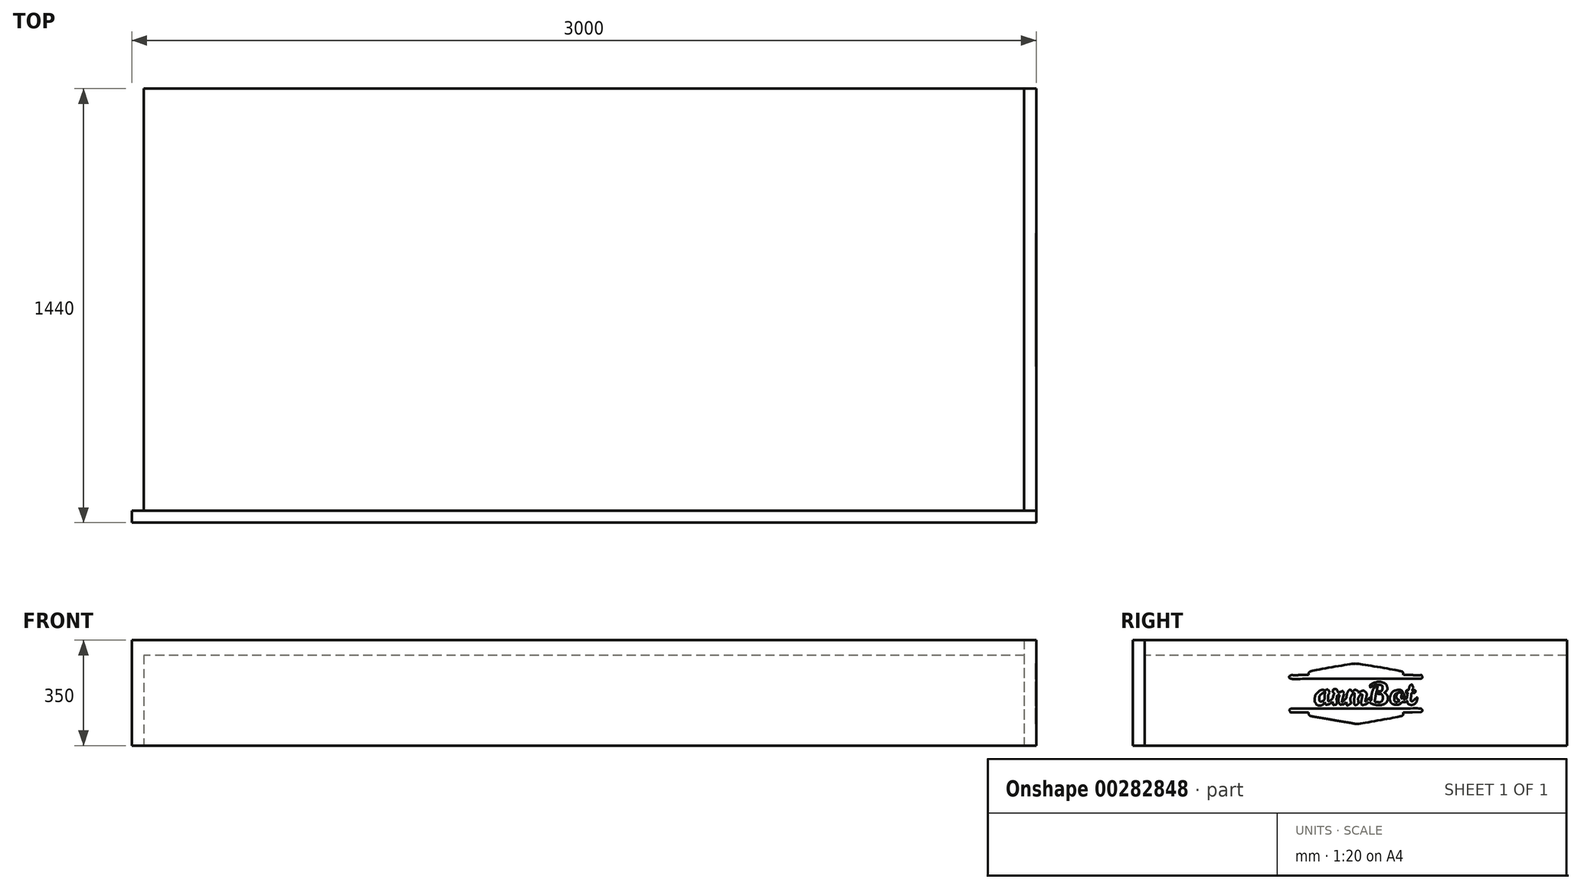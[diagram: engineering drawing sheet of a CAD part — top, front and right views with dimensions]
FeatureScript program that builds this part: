
annotation { "Feature Type Name" : "Feature", "Feature Type Description" : "" }
export const myFeature = defineFeature(function(context is Context, id is Id, definition is map)
    precondition{}
    {
        {
            var Q0;
            Q0=qCreatedBy(makeId("Top.planeOp"),FACE);
            var sketch = newSketch(context, id + "F0", { "sketchPlane" : qUnion([Q0])});
            skLineSegment(sketch, "E0.bottom", {"start": v(1460, 700) * mm, "end": v(-1460, 700) * mm});
            skLineSegment(sketch, "E0.top", {"start": v(1460, -700) * mm, "end": v(-1460, -700) * mm});
            skLineSegment(sketch, "E0.left", {"start": v(1460, 700) * mm, "end": v(1460, -700) * mm});
            skLineSegment(sketch, "E0.right", {"start": v(-1460, 700) * mm, "end": v(-1460, -700) * mm});
            skPoint(sketch, "E0.middle", {"position": v(0, 0) * mm});
            skSolve(sketch);
        }
        {
            var Q0;
            Q0=qSketchRegion(id+"F0",true);
            extrude(context, id + "F1", {"entities" : qUnion([Q0]), "depth" : 300 * mm});
        }
        {
            var Q0;
            Q0=makeQuery(id+"F1.opExtrude","SWEPT_FACE",FACE,{"disambiguationData":[OSD([sQuery(id+"F0.wireOp",EDGE,"E0.left")])]});
            var sketch = newSketch(context, id + "F2", { "sketchPlane" : qUnion([Q0])});
            skLineSegment(sketch, "E1.bottom", {"start": v(-700, 0) * mm, "end": v(700, 0) * mm});
            skLineSegment(sketch, "E1.top", {"start": v(-700, 350) * mm, "end": v(700, 350) * mm});
            skLineSegment(sketch, "E1.left", {"start": v(-700, 0) * mm, "end": v(-700, 350) * mm});
            skLineSegment(sketch, "E1.right", {"start": v(700, 0) * mm, "end": v(700, 350) * mm});
            skSolve(sketch);
        }
        {
            var Q0;
            Q0=qSketchRegion(id+"F2",true);
            extrude(context, id + "F3", {"entities" : qUnion([Q0]), "depth" : 40 * mm});
        }
        {
            var Q0;
            Q0=makeQuery(id+"F1.opExtrude","SWEPT_FACE",FACE,{"disambiguationData":[OSD([sQuery(id+"F0.wireOp",EDGE,"E0.top")])]});
            var sketch = newSketch(context, id + "F4", { "sketchPlane" : qUnion([Q0])});
            skLineSegment(sketch, "E2.bottom", {"start": v(-1500, 350) * mm, "end": v(1500, 350) * mm});
            skLineSegment(sketch, "E2.top", {"start": v(-1500, 0) * mm, "end": v(1500, 0) * mm});
            skLineSegment(sketch, "E2.left", {"start": v(-1500, 350) * mm, "end": v(-1500, 0) * mm});
            skLineSegment(sketch, "E2.right", {"start": v(1500, 350) * mm, "end": v(1500, 0) * mm});
            skSolve(sketch);
        }
        {
            var Q0;
            Q0=qSketchRegion(id+"F4",true);
            extrude(context, id + "F5", {"entities" : qUnion([Q0]), "depth" : 40 * mm});
        }
        {
            var Q0;
            Q0=makeQuery(id+"F1.opExtrude","CAP_FACE",FACE,{"disambiguationData":[OSD([sQuery(id+"F0.wireOp",EDGE,"E0.bottom"),sQuery(id+"F0.wireOp",EDGE,"E0.top"),sQuery(id+"F0.wireOp",EDGE,"E0.left"),sQuery(id+"F0.wireOp",EDGE,"E0.right")])],"isStart":false});
            var sketch = newSketch(context, id + "F6", { "sketchPlane" : qUnion([Q0])});
            skFitSpline(sketch, "E3", {"points": [v(-9.76, -247.93) * mm, v(-14.36, -247) * mm, v(-98.7, -232.48) * mm, v(-197.18, -215.67) * mm]});
            skFitSpline(sketch, "E4", {"points": [v(-197.18, -215.67) * mm, v(-303.5, -197.52) * mm, v(-377.79, -184.02) * mm, v(-380.05, -182.43) * mm]});
            skFitSpline(sketch, "E5", {"points": [v(-380.05, -182.43) * mm, v(-386.35, -178.01) * mm, v(-389.22, -172.54) * mm, v(-390.38, -162.7) * mm]});
            skLineSegment(sketch, "E6", {"start": v(-390.38, -162.7) * mm, "end": v(-391.49, -153.38) * mm});
            skLineSegment(sketch, "E7", {"start": v(-391.49, -153.38) * mm, "end": v(-463.29, -153.35) * mm});
            skFitSpline(sketch, "E8", {"points": [v(-463.29, -153.35) * mm, v(-540.74, -153.32) * mm, v(-542.21, -153.15) * mm, v(-546.84, -143.5) * mm]});
            skFitSpline(sketch, "E9", {"points": [v(-546.84, -143.5) * mm, v(-550.32, -136.23) * mm, v(-547.5, -129.03) * mm, v(-539.62, -125.02) * mm]});
            skFitSpline(sketch, "E10", {"points": [v(-539.62, -125.02) * mm, v(-533.58, -121.95) * mm, v(-503.94, -121.77) * mm, v(0.65, -121.77) * mm]});
            skFitSpline(sketch, "E11", {"points": [v(0.65, -121.77) * mm, v(385.66, -121.76) * mm, v(536.18, -122.34) * mm, v(540.43, -123.82) * mm]});
            skFitSpline(sketch, "E12", {"points": [v(540.43, -123.82) * mm, v(543.67, -124.95) * mm, v(547.14, -127.4) * mm, v(548.14, -129.27) * mm]});
            skFitSpline(sketch, "E13", {"points": [v(548.14, -129.27) * mm, v(551.05, -134.7) * mm, v(550.26, -143.3) * mm, v(546.41, -148.06) * mm]});
            skLineSegment(sketch, "E14", {"start": v(546.41, -148.06) * mm, "end": v(542.86, -152.45) * mm});
            skLineSegment(sketch, "E15", {"start": v(542.86, -152.45) * mm, "end": v(467.85, -153.38) * mm});
            skLineSegment(sketch, "E16", {"start": v(467.85, -153.38) * mm, "end": v(392.83, -154.3) * mm});
            skLineSegment(sketch, "E17", {"start": v(392.83, -154.3) * mm, "end": v(392.5, -162.05) * mm});
            skFitSpline(sketch, "E18", {"points": [v(392.5, -162.05) * mm, v(391.99, -173.78) * mm, v(387.68, -180.46) * mm, v(378.46, -183.85) * mm]});
            skFitSpline(sketch, "E19", {"points": [v(378.46, -183.85) * mm, v(371.97, -186.24) * mm, v(2.57, -250.58) * mm, v(-0.47, -249.85) * mm]});
            skFitSpline(sketch, "E20", {"points": [v(-0.47, -249.85) * mm, v(-0.98, -249.73) * mm, v(-5.16, -248.87) * mm, v(-9.76, -247.93) * mm]});
            skLineSegment(sketch, "E21", {"start": v(-9.76, -247.93) * mm, "end": v(-9.76, -247.93) * mm});
            skFitSpline(sketch, "E22", {"points": [v(163.18, -91.34) * mm, v(144.56, -86.99) * mm, v(127.82, -80.58) * mm, v(118.25, -74.15) * mm]});
            skLineSegment(sketch, "E23", {"start": v(118.25, -74.15) * mm, "end": v(108.82, -67.8) * mm});
            skLineSegment(sketch, "E24", {"start": v(108.82, -67.8) * mm, "end": v(101.7, -74.22) * mm});
            skFitSpline(sketch, "E25", {"points": [v(101.7, -74.22) * mm, v(92.92, -82.15) * mm, v(86.06, -85.78) * mm, v(75.22, -88.2) * mm]});
            skFitSpline(sketch, "E26", {"points": [v(75.22, -88.2) * mm, v(52.86, -93.22) * mm, v(44.33, -75.76) * mm, v(50.52, -37.64) * mm]});
            skFitSpline(sketch, "E27", {"points": [v(50.52, -37.64) * mm, v(54.63, -12.34) * mm, v(54.44, -8.7) * mm, v(48.9, -6.17) * mm]});
            skFitSpline(sketch, "E28", {"points": [v(48.9, -6.17) * mm, v(42.7, -3.35) * mm, v(36.64, -7.44) * mm, v(29.87, -18.99) * mm]});
            skFitSpline(sketch, "E29", {"points": [v(29.87, -18.99) * mm, v(21.01, -34.1) * mm, v(18.43, -44.15) * mm, v(20.53, -55.3) * mm]});
            skFitSpline(sketch, "E30", {"points": [v(20.53, -55.3) * mm, v(21.54, -60.66) * mm, v(22.46, -68.35) * mm, v(22.57, -72.38) * mm]});
            skFitSpline(sketch, "E31", {"points": [v(22.57, -72.38) * mm, v(22.76, -78.97) * mm, v(22, -80.26) * mm, v(14.95, -85.23) * mm]});
            skFitSpline(sketch, "E32", {"points": [v(14.95, -85.23) * mm, v(4.39, -92.68) * mm, v(-7.54, -93.24) * mm, v(-11.04, -86.43) * mm]});
            skFitSpline(sketch, "E33", {"points": [v(-11.04, -86.43) * mm, v(-13.95, -80.76) * mm, v(-14.16, -56.28) * mm, v(-11.54, -26.93) * mm]});
            skFitSpline(sketch, "E34", {"points": [v(-11.54, -26.93) * mm, v(-9.2, -0.66) * mm, v(-9.84, 2.83) * mm, v(-17.07, 2.83) * mm]});
            skFitSpline(sketch, "E35", {"points": [v(-17.07, 2.83) * mm, v(-23.9, 2.83) * mm, v(-30.46, -4.7) * mm, v(-38.87, -22.23) * mm]});
            skFitSpline(sketch, "E36", {"points": [v(-38.87, -22.23) * mm, v(-45.93, -36.93) * mm, v(-46.62, -45.33) * mm, v(-42.27, -63.77) * mm]});
            skFitSpline(sketch, "E37", {"points": [v(-42.27, -63.77) * mm, v(-38.91, -78.01) * mm, v(-39.9, -80.3) * mm, v(-52.19, -87) * mm]});
            skFitSpline(sketch, "E38", {"points": [v(-52.19, -87) * mm, v(-68.26, -95.75) * mm, v(-75.2, -92.86) * mm, v(-77.56, -76.43) * mm]});
            skLineSegment(sketch, "E39", {"start": v(-77.56, -76.43) * mm, "end": v(-78.86, -67.36) * mm});
            skLineSegment(sketch, "E40", {"start": v(-78.86, -67.36) * mm, "end": v(-86.62, -74.83) * mm});
            skFitSpline(sketch, "E41", {"points": [v(-86.62, -74.83) * mm, v(-97.05, -84.9) * mm, v(-104.92, -88.54) * mm, v(-116.78, -88.82) * mm]});
            skFitSpline(sketch, "E42", {"points": [v(-116.78, -88.82) * mm, v(-128.34, -89.1) * mm, v(-132.94, -86) * mm, v(-138.3, -74.35) * mm]});
            skFitSpline(sketch, "E43", {"points": [v(-138.3, -74.35) * mm, v(-144.12, -61.65) * mm, v(-141.58, -31.54) * mm, v(-133.32, -15.58) * mm]});
            skLineSegment(sketch, "E44", {"start": v(-133.32, -15.58) * mm, "end": v(-130.44, -10) * mm});
            skLineSegment(sketch, "E45", {"start": v(-130.44, -10) * mm, "end": v(-141.2, -10.56) * mm});
            skLineSegment(sketch, "E46", {"start": v(-141.2, -10.56) * mm, "end": v(-151.94, -11.12) * mm});
            skLineSegment(sketch, "E47", {"start": v(-151.94, -11.12) * mm, "end": v(-155.34, -25.07) * mm});
            skFitSpline(sketch, "E48", {"points": [v(-155.34, -25.07) * mm, v(-157.97, -35.9) * mm, v(-158.52, -43.56) * mm, v(-157.8, -59.34) * mm]});
            skFitSpline(sketch, "E49", {"points": [v(-157.8, -59.34) * mm, v(-157.29, -70.85) * mm, v(-157.67, -81.12) * mm, v(-158.7, -83.03) * mm]});
            skFitSpline(sketch, "E50", {"points": [v(-158.7, -83.03) * mm, v(-161.25, -87.81) * mm, v(-170.24, -92.01) * mm, v(-177.92, -92.01) * mm]});
            skFitSpline(sketch, "E51", {"points": [v(-177.92, -92.01) * mm, v(-186.08, -92.01) * mm, v(-189.42, -87.45) * mm, v(-191.2, -73.87) * mm]});
            skLineSegment(sketch, "E52", {"start": v(-191.2, -73.87) * mm, "end": v(-192.48, -64.09) * mm});
            skLineSegment(sketch, "E53", {"start": v(-192.48, -64.09) * mm, "end": v(-200.42, -71.4) * mm});
            skFitSpline(sketch, "E54", {"points": [v(-200.42, -71.4) * mm, v(-209.89, -80.13) * mm, v(-220.17, -85.65) * mm, v(-231.87, -88.27) * mm]});
            skFitSpline(sketch, "E55", {"points": [v(-231.87, -88.27) * mm, v(-243.7, -90.92) * mm, v(-250.08, -87.49) * mm, v(-254.4, -76.16) * mm]});
            skLineSegment(sketch, "E56", {"start": v(-254.4, -76.16) * mm, "end": v(-257.65, -67.68) * mm});
            skLineSegment(sketch, "E57", {"start": v(-257.65, -67.68) * mm, "end": v(-262.94, -74.1) * mm});
            skFitSpline(sketch, "E58", {"points": [v(-262.94, -74.1) * mm, v(-279.38, -94.04) * mm, v(-316.37, -95.84) * mm, v(-331.85, -77.45) * mm]});
            skFitSpline(sketch, "E59", {"points": [v(-331.85, -77.45) * mm, v(-339.17, -68.75) * mm, v(-341.42, -59.86) * mm, v(-340.14, -44.75) * mm]});
            skFitSpline(sketch, "E60", {"points": [v(-340.14, -44.75) * mm, v(-338.13, -20.94) * mm, v(-329.14, -1.86) * mm, v(-313.1, 12.61) * mm]});
            skFitSpline(sketch, "E61", {"points": [v(-313.1, 12.61) * mm, v(-297.94, 26.32) * mm, v(-276.95, 32.69) * mm, v(-259.7, 28.82) * mm]});
            skFitSpline(sketch, "E62", {"points": [v(-259.7, 28.82) * mm, v(-252.55, 27.22) * mm, v(-250.45, 27.38) * mm, v(-247.85, 29.73) * mm]});
            skFitSpline(sketch, "E63", {"points": [v(-247.85, 29.73) * mm, v(-240.93, 36) * mm, v(-226.99, 30.32) * mm, v(-220.73, 18.7) * mm]});
            skLineSegment(sketch, "E64", {"start": v(-220.73, 18.7) * mm, "end": v(-217.21, 12.17) * mm});
            skLineSegment(sketch, "E65", {"start": v(-217.21, 12.17) * mm, "end": v(-223.2, 0.02) * mm});
            skFitSpline(sketch, "E66", {"points": [v(-223.2, 0.02) * mm, v(-228.92, -11.58) * mm, v(-229.19, -13.1) * mm, v(-229.16, -33.94) * mm]});
            skFitSpline(sketch, "E67", {"points": [v(-229.16, -33.94) * mm, v(-229.13, -57.9) * mm, v(-228.1, -61.48) * mm, v(-221.81, -59.49) * mm]});
            skFitSpline(sketch, "E68", {"points": [v(-221.81, -59.49) * mm, v(-215.07, -57.35) * mm, v(-188.28, -30.28) * mm, v(-188.28, -25.6) * mm]});
            skFitSpline(sketch, "E69", {"points": [v(-188.28, -25.6) * mm, v(-188.28, -23.36) * mm, v(-186.22, -15.85) * mm, v(-183.7, -8.92) * mm]});
            skFitSpline(sketch, "E70", {"points": [v(-183.7, -8.92) * mm, v(-179.26, 3.33) * mm, v(-179.23, 3.78) * mm, v(-182.54, 7.44) * mm]});
            skFitSpline(sketch, "E71", {"points": [v(-182.54, 7.44) * mm, v(-188.48, 13.98) * mm, v(-190.53, 19.67) * mm, v(-189.3, 26.21) * mm]});
            skFitSpline(sketch, "E72", {"points": [v(-189.3, 26.21) * mm, v(-187.82, 34.15) * mm, v(-182.12, 38.16) * mm, v(-172.31, 38.16) * mm]});
            skFitSpline(sketch, "E73", {"points": [v(-172.31, 38.16) * mm, v(-163.16, 38.16) * mm, v(-156.23, 32.34) * mm, v(-150.73, 20.03) * mm]});
            skFitSpline(sketch, "E74", {"points": [v(-150.73, 20.03) * mm, v(-147.7, 13.24) * mm, v(-146.4, 12.12) * mm, v(-141.55, 12.12) * mm]});
            skFitSpline(sketch, "E75", {"points": [v(-141.55, 12.12) * mm, v(-138.45, 12.12) * mm, v(-130.4, 14.33) * mm, v(-123.66, 17.03) * mm]});
            skFitSpline(sketch, "E76", {"points": [v(-123.66, 17.03) * mm, v(-109.3, 22.78) * mm, v(-107.41, 22.17) * mm, v(-101.2, 9.8) * mm]});
            skLineSegment(sketch, "E77", {"start": v(-101.2, 9.8) * mm, "end": v(-96.87, 1.18) * mm});
            skLineSegment(sketch, "E78", {"start": v(-96.87, 1.18) * mm, "end": v(-104.6, -26.95) * mm});
            skFitSpline(sketch, "E79", {"points": [v(-104.6, -26.95) * mm, v(-115.26, -65.72) * mm, v(-113.52, -68.38) * mm, v(-91.12, -47.46) * mm]});
            skLineSegment(sketch, "E80", {"start": v(-91.12, -47.46) * mm, "end": v(-77.26, -34.51) * mm});
            skLineSegment(sketch, "E81", {"start": v(-77.26, -34.51) * mm, "end": v(-76.15, -22.7) * mm});
            skFitSpline(sketch, "E82", {"points": [v(-76.15, -22.7) * mm, v(-74.76, -7.77) * mm, v(-68.68, 10.87) * mm, v(-61.04, 23.61) * mm]});
            skFitSpline(sketch, "E83", {"points": [v(-61.04, 23.61) * mm, v(-56.21, 31.68) * mm, v(-54.07, 33.61) * mm, v(-49.45, 34.07) * mm]});
            skFitSpline(sketch, "E84", {"points": [v(-49.45, 34.07) * mm, v(-44.95, 34.52) * mm, v(-42.63, 33.32) * mm, v(-38.15, 28.2) * mm]});
            skFitSpline(sketch, "E85", {"points": [v(-38.15, 28.2) * mm, v(-35.04, 24.67) * mm, v(-32.16, 20.74) * mm, v(-31.73, 19.46) * mm]});
            skFitSpline(sketch, "E86", {"points": [v(-31.73, 19.46) * mm, v(-31.21, 17.9) * mm, v(-28.37, 19.02) * mm, v(-23, 22.9) * mm]});
            skFitSpline(sketch, "E87", {"points": [v(-23, 22.9) * mm, v(-11.96, 30.9) * mm, v(-1.17, 32.3) * mm, v(9.54, 27.1) * mm]});
            skFitSpline(sketch, "E88", {"points": [v(9.54, 27.1) * mm, v(18.23, 22.9) * mm, v(22.7, 17.7) * mm, v(24.79, 9.4) * mm]});
            skLineSegment(sketch, "E89", {"start": v(24.79, 9.4) * mm, "end": v(26.04, 4.44) * mm});
            skLineSegment(sketch, "E90", {"start": v(26.04, 4.44) * mm, "end": v(30.92, 9.1) * mm});
            skFitSpline(sketch, "E91", {"points": [v(30.92, 9.1) * mm, v(43.6, 21.22) * mm, v(66.06, 25.1) * mm, v(77.8, 17.18) * mm]});
            skFitSpline(sketch, "E92", {"points": [v(77.8, 17.18) * mm, v(81.26, 14.85) * mm, v(85.14, 10.88) * mm, v(86.42, 8.35) * mm]});
            skFitSpline(sketch, "E93", {"points": [v(86.42, 8.35) * mm, v(90.04, 1.18) * mm, v(89.21, -14.95) * mm, v(84.14, -35.88) * mm]});
            skFitSpline(sketch, "E94", {"points": [v(84.14, -35.88) * mm, v(81.59, -46.43) * mm, v(79.5, -56.26) * mm, v(79.5, -57.73) * mm]});
            skFitSpline(sketch, "E95", {"points": [v(79.5, -57.73) * mm, v(79.5, -63.6) * mm, v(86.26, -59.69) * mm, v(100.97, -45.33) * mm]});
            skFitSpline(sketch, "E96", {"points": [v(100.97, -45.33) * mm, v(110.63, -35.9) * mm, v(117.25, -30.77) * mm, v(118.65, -31.64) * mm]});
            skFitSpline(sketch, "E97", {"points": [v(118.65, -31.64) * mm, v(120.17, -32.58) * mm, v(120.56, -36.5) * mm, v(119.89, -43.92) * mm]});
            skFitSpline(sketch, "E98", {"points": [v(119.89, -43.92) * mm, v(118.95, -54.29) * mm, v(119.1, -54.82) * mm, v(123.1, -54.82) * mm]});
            skFitSpline(sketch, "E99", {"points": [v(123.1, -54.82) * mm, v(127.02, -54.82) * mm, v(127.36, -53.84) * mm, v(128.4, -39.48) * mm]});
            skFitSpline(sketch, "E100", {"points": [v(128.4, -39.48) * mm, v(130.72, -7.09) * mm, v(148.03, 43.77) * mm, v(160.6, 55.09) * mm]});
            skFitSpline(sketch, "E101", {"points": [v(160.6, 55.09) * mm, v(178.01, 70.78) * mm, v(179.9, 58.14) * mm, v(168.42, 2.83) * mm]});
            skFitSpline(sketch, "E102", {"points": [v(168.42, 2.83) * mm, v(163.73, -19.8) * mm, v(158.67, -63.5) * mm, v(160.5, -65.68) * mm]});
            skFitSpline(sketch, "E103", {"points": [v(160.5, -65.68) * mm, v(161.76, -67.18) * mm, v(175.96, -69.61) * mm, v(183.63, -69.64) * mm]});
            skFitSpline(sketch, "E104", {"points": [v(183.63, -69.64) * mm, v(200.98, -69.71) * mm, v(215.69, -61.64) * mm, v(220.83, -49.22) * mm]});
            skFitSpline(sketch, "E105", {"points": [v(220.83, -49.22) * mm, v(224.51, -40.34) * mm, v(222.43, -16.02) * mm, v(217.28, -7.68) * mm]});
            skFitSpline(sketch, "E106", {"points": [v(217.28, -7.68) * mm, v(213.13, -0.96) * mm, v(212.95, -0.9) * mm, v(200.63, -0.9) * mm]});
            skFitSpline(sketch, "E107", {"points": [v(200.63, -0.9) * mm, v(187.27, -0.9) * mm, v(181.1, 1.8) * mm, v(179.39, 8.35) * mm]});
            skFitSpline(sketch, "E108", {"points": [v(179.39, 8.35) * mm, v(178.82, 10.5) * mm, v(179.82, 13.89) * mm, v(181.7, 16.2) * mm]});
            skFitSpline(sketch, "E109", {"points": [v(181.7, 16.2) * mm, v(184.4, 19.56) * mm, v(187.56, 20.46) * mm, v(199.63, 21.31) * mm]});
            skFitSpline(sketch, "E110", {"points": [v(199.63, 21.31) * mm, v(213.63, 22.3) * mm, v(214.4, 22.6) * mm, v(217.02, 27.93) * mm]});
            skFitSpline(sketch, "E111", {"points": [v(217.02, 27.93) * mm, v(218.53, 31) * mm, v(219.77, 38.53) * mm, v(219.78, 44.67) * mm]});
            skFitSpline(sketch, "E112", {"points": [v(219.78, 44.67) * mm, v(219.8, 64.17) * mm, v(211.17, 71.67) * mm, v(187.07, 73.1) * mm]});
            skFitSpline(sketch, "E113", {"points": [v(187.07, 73.1) * mm, v(170.05, 74.11) * mm, v(157.7, 71.45) * mm, v(139.99, 62.97) * mm]});
            skFitSpline(sketch, "E114", {"points": [v(139.99, 62.97) * mm, v(124.82, 55.7) * mm, v(118.55, 54.98) * mm, v(118.55, 60.51) * mm]});
            skFitSpline(sketch, "E115", {"points": [v(118.55, 60.51) * mm, v(118.55, 70.5) * mm, v(143.11, 88.38) * mm, v(165.9, 94.95) * mm]});
            skFitSpline(sketch, "E116", {"points": [v(165.9, 94.95) * mm, v(181.16, 99.36) * mm, v(211.58, 97.92) * mm, v(227.33, 92.04) * mm]});
            skFitSpline(sketch, "E117", {"points": [v(227.33, 92.04) * mm, v(241.91, 86.6) * mm, v(254.67, 73.92) * mm, v(257.71, 61.83) * mm]});
            skFitSpline(sketch, "E118", {"points": [v(257.71, 61.83) * mm, v(262.48, 42.9) * mm, v(259.33, 31.38) * mm, v(245.79, 18.17) * mm]});
            skFitSpline(sketch, "E119", {"points": [v(245.79, 18.17) * mm, v(240.28, 12.8) * mm, v(236.48, 8.4) * mm, v(237.34, 8.4) * mm]});
            skFitSpline(sketch, "E120", {"points": [v(237.34, 8.4) * mm, v(241.01, 8.4) * mm, v(256.17, -7.19) * mm, v(259.81, -14.71) * mm]});
            skFitSpline(sketch, "E121", {"points": [v(259.81, -14.71) * mm, v(265.46, -26.39) * mm, v(265.68, -49.04) * mm, v(260.25, -59.68) * mm]});
            skFitSpline(sketch, "E122", {"points": [v(260.25, -59.68) * mm, v(254.38, -71.16) * mm, v(239.5, -83.55) * mm, v(225.92, -88.28) * mm]});
            skFitSpline(sketch, "E123", {"points": [v(225.92, -88.28) * mm, v(211.44, -93.33) * mm, v(178.53, -94.93) * mm, v(163.18, -91.34) * mm]});
            skFitSpline(sketch, "E124", {"points": [v(-281.84, -62.14) * mm, v(-267.85, -56.85) * mm, v(-259.05, -41.8) * mm, v(-258.98, -23.08) * mm]});
            skFitSpline(sketch, "E125", {"points": [v(-258.98, -23.08) * mm, v(-258.96, -16.37) * mm, v(-258.05, -6.04) * mm, v(-256.95, -0.12) * mm]});
            skFitSpline(sketch, "E126", {"points": [v(-256.95, -0.12) * mm, v(-255.86, 5.8) * mm, v(-255.42, 11.09) * mm, v(-255.98, 11.64) * mm]});
            skFitSpline(sketch, "E127", {"points": [v(-255.98, 11.64) * mm, v(-257.93, 13.6) * mm, v(-273.99, 6.15) * mm, v(-282.7, -0.75) * mm]});
            skFitSpline(sketch, "E128", {"points": [v(-282.7, -0.75) * mm, v(-295.24, -10.66) * mm, v(-302.1, -24.16) * mm, v(-303.18, -41.06) * mm]});
            skFitSpline(sketch, "E129", {"points": [v(-303.18, -41.06) * mm, v(-303.98, -53.62) * mm, v(-303.72, -54.84) * mm, v(-299.24, -59.32) * mm]});
            skFitSpline(sketch, "E130", {"points": [v(-299.24, -59.32) * mm, v(-294.03, -64.53) * mm, v(-289.93, -65.2) * mm, v(-281.84, -62.14) * mm]});
            skFitSpline(sketch, "E131", {"points": [v(-459.3, -89.94) * mm, v(-464.48, -84.62) * mm, v(-460.7, -35.47) * mm, v(-453.32, -12.23) * mm]});
            skFitSpline(sketch, "E132", {"points": [v(-453.32, -12.23) * mm, v(-452.15, -8.52) * mm, v(-452.73, -8.33) * mm, v(-465.23, -8.33) * mm]});
            skFitSpline(sketch, "E133", {"points": [v(-465.23, -8.33) * mm, v(-476.68, -8.33) * mm, v(-478.37, -7.9) * mm, v(-478.37, -4.96) * mm]});
            skFitSpline(sketch, "E134", {"points": [v(-478.37, -4.96) * mm, v(-478.37, 0.26) * mm, v(-468.99, 8.03) * mm, v(-457.1, 12.63) * mm]});
            skLineSegment(sketch, "E135", {"start": v(-457.1, 12.63) * mm, "end": v(-446.32, 16.8) * mm});
            skLineSegment(sketch, "E136", {"start": v(-446.32, 16.8) * mm, "end": v(-438.43, 39.1) * mm});
            skFitSpline(sketch, "E137", {"points": [v(-438.43, 39.1) * mm, v(-434.08, 51.37) * mm, v(-429.87, 62.96) * mm, v(-429.07, 64.87) * mm]});
            skFitSpline(sketch, "E138", {"points": [v(-429.07, 64.87) * mm, v(-427.72, 68.05) * mm, v(-428.28, 68.22) * mm, v(-435.78, 67) * mm]});
            skFitSpline(sketch, "E139", {"points": [v(-435.78, 67) * mm, v(-447.95, 65.04) * mm, v(-458.5, 59.86) * mm, v(-467.75, 51.34) * mm]});
            skFitSpline(sketch, "E140", {"points": [v(-467.75, 51.34) * mm, v(-479.66, 40.36) * mm, v(-483.95, 41.51) * mm, v(-483.95, 55.7) * mm]});
            skFitSpline(sketch, "E141", {"points": [v(-483.95, 55.7) * mm, v(-483.95, 68.83) * mm, v(-467.73, 83.32) * mm, v(-445.28, 90.26) * mm]});
            skFitSpline(sketch, "E142", {"points": [v(-445.28, 90.26) * mm, v(-427.1, 95.87) * mm, v(-406.05, 97.33) * mm, v(-358.74, 96.25) * mm]});
            skFitSpline(sketch, "E143", {"points": [v(-358.74, 96.25) * mm, v(-311.18, 95.17) * mm, v(-311.95, 95.43) * mm, v(-317.58, 82.22) * mm]});
            skFitSpline(sketch, "E144", {"points": [v(-317.58, 82.22) * mm, v(-323.64, 68.03) * mm, v(-324, 67.91) * mm, v(-360.96, 67.88) * mm]});
            skLineSegment(sketch, "E145", {"start": v(-360.96, 67.88) * mm, "end": v(-393.76, 67.85) * mm});
            skLineSegment(sketch, "E146", {"start": v(-393.76, 67.85) * mm, "end": v(-398.66, 47.9) * mm});
            skFitSpline(sketch, "E147", {"points": [v(-398.66, 47.9) * mm, v(-401.36, 36.91) * mm, v(-403.87, 26.67) * mm, v(-404.24, 25.14) * mm]});
            skFitSpline(sketch, "E148", {"points": [v(-404.24, 25.14) * mm, v(-404.8, 22.8) * mm, v(-401.23, 22.27) * mm, v(-381.74, 21.83) * mm]});
            skFitSpline(sketch, "E149", {"points": [v(-381.74, 21.83) * mm, v(-367.15, 21.5) * mm, v(-358.1, 20.53) * mm, v(-357.28, 19.21) * mm]});
            skFitSpline(sketch, "E150", {"points": [v(-357.28, 19.21) * mm, v(-355.76, 16.75) * mm, v(-359.89, 2.02) * mm, v(-363.24, -2.01) * mm]});
            skFitSpline(sketch, "E151", {"points": [v(-363.24, -2.01) * mm, v(-365.2, -4.38) * mm, v(-369.3, -4.62) * mm, v(-389.06, -3.54) * mm]});
            skLineSegment(sketch, "E152", {"start": v(-389.06, -3.54) * mm, "end": v(-412.56, -2.27) * mm});
            skLineSegment(sketch, "E153", {"start": v(-412.56, -2.27) * mm, "end": v(-416.52, -18.78) * mm});
            skFitSpline(sketch, "E154", {"points": [v(-416.52, -18.78) * mm, v(-421.04, -37.64) * mm, v(-423.77, -53.93) * mm, v(-425.45, -72.08) * mm]});
            skFitSpline(sketch, "E155", {"points": [v(-425.45, -72.08) * mm, v(-426.44, -82.86) * mm, v(-427.3, -85.14) * mm, v(-431.33, -87.78) * mm]});
            skFitSpline(sketch, "E156", {"points": [v(-431.33, -87.78) * mm, v(-437.41, -91.77) * mm, v(-456.13, -93.2) * mm, v(-459.3, -89.94) * mm]});
            skFitSpline(sketch, "E157", {"points": [v(317.5, -88.5) * mm, v(302.9, -83.79) * mm, v(289.51, -71.3) * mm, v(285.81, -58.96) * mm]});
            skFitSpline(sketch, "E158", {"points": [v(285.81, -58.96) * mm, v(282.17, -46.8) * mm, v(284.25, -22.14) * mm, v(289.96, -9.87) * mm]});
            skFitSpline(sketch, "E159", {"points": [v(289.96, -9.87) * mm, v(299.26, 10.12) * mm, v(316.09, 24.32) * mm, v(335.9, 28.9) * mm]});
            skFitSpline(sketch, "E160", {"points": [v(335.9, 28.9) * mm, v(354.07, 33.1) * mm, v(378.44, 28.13) * mm, v(386.33, 18.63) * mm]});
            skFitSpline(sketch, "E161", {"points": [v(386.33, 18.63) * mm, v(390.02, 14.18) * mm, v(386.8, 12.82) * mm, v(369.86, 11.65) * mm]});
            skFitSpline(sketch, "E162", {"points": [v(369.86, 11.65) * mm, v(362, 11.12) * mm, v(352.6, 9.43) * mm, v(348.96, 7.91) * mm]});
            skFitSpline(sketch, "E163", {"points": [v(348.96, 7.91) * mm, v(331.95, 0.8) * mm, v(320.77, -16.17) * mm, v(320.52, -35.3) * mm]});
            skFitSpline(sketch, "E164", {"points": [v(320.52, -35.3) * mm, v(320.22, -57.93) * mm, v(334.52, -68.41) * mm, v(357.15, -62.13) * mm]});
            skLineSegment(sketch, "E165", {"start": v(357.15, -62.13) * mm, "end": v(364.23, -60.16) * mm});
            skLineSegment(sketch, "E166", {"start": v(364.23, -60.16) * mm, "end": v(357.84, -53.09) * mm});
            skFitSpline(sketch, "E167", {"points": [v(357.84, -53.09) * mm, v(336.45, -29.41) * mm, v(349.03, 6.55) * mm, v(378.7, 6.55) * mm]});
            skFitSpline(sketch, "E168", {"points": [v(378.7, 6.55) * mm, v(389.23, 6.55) * mm, v(395.06, 3.8) * mm, v(399.43, -3.17) * mm]});
            skFitSpline(sketch, "E169", {"points": [v(399.43, -3.17) * mm, v(402.65, -8.3) * mm, v(403.12, -11.47) * mm, v(402.44, -23.2) * mm]});
            skFitSpline(sketch, "E170", {"points": [v(402.44, -23.2) * mm, v(402, -30.88) * mm, v(401.02, -39.04) * mm, v(400.27, -41.34) * mm]});
            skFitSpline(sketch, "E171", {"points": [v(400.27, -41.34) * mm, v(398.58, -46.51) * mm, v(402.33, -46.92) * mm, v(411.06, -42.52) * mm]});
            skFitSpline(sketch, "E172", {"points": [v(411.06, -42.52) * mm, v(421.31, -37.33) * mm, v(425.37, -32.45) * mm, v(425.44, -25.2) * mm]});
            skFitSpline(sketch, "E173", {"points": [v(425.44, -25.2) * mm, v(425.48, -21.55) * mm, v(426.6, -12.92) * mm, v(427.94, -6.02) * mm]});
            skFitSpline(sketch, "E174", {"points": [v(427.94, -6.02) * mm, v(429.27, 0.87) * mm, v(429.94, 6.94) * mm, v(429.42, 7.46) * mm]});
            skFitSpline(sketch, "E175", {"points": [v(429.42, 7.46) * mm, v(428.9, 7.98) * mm, v(425.6, 8.4) * mm, v(422.07, 8.4) * mm]});
            skFitSpline(sketch, "E176", {"points": [v(422.07, 8.4) * mm, v(415.71, 8.4) * mm, v(415.67, 8.46) * mm, v(416.93, 15.14) * mm]});
            skFitSpline(sketch, "E177", {"points": [v(416.93, 15.14) * mm, v(418.93, 25.81) * mm, v(421.68, 28.86) * mm, v(429.3, 28.86) * mm]});
            skFitSpline(sketch, "E178", {"points": [v(429.3, 28.86) * mm, v(435.8, 28.86) * mm, v(436.17, 29.23) * mm, v(439.97, 39.55) * mm]});
            skFitSpline(sketch, "E179", {"points": [v(439.97, 39.55) * mm, v(450.84, 69.05) * mm, v(465.01, 75.94) * mm, v(473.83, 56) * mm]});
            skLineSegment(sketch, "E180", {"start": v(473.83, 56) * mm, "end": v(477.45, 47.84) * mm});
            skLineSegment(sketch, "E181", {"start": v(477.45, 47.84) * mm, "end": v(472.82, 39.75) * mm});
            skFitSpline(sketch, "E182", {"points": [v(472.82, 39.75) * mm, v(470.27, 35.3) * mm, v(468.18, 31.02) * mm, v(468.17, 30.25) * mm]});
            skFitSpline(sketch, "E183", {"points": [v(468.17, 30.25) * mm, v(468.15, 29.49) * mm, v(474, 28.86) * mm, v(481.16, 28.86) * mm]});
            skFitSpline(sketch, "E184", {"points": [v(481.16, 28.86) * mm, v(493.59, 28.86) * mm, v(494.18, 28.66) * mm, v(494.18, 24.49) * mm]});
            skFitSpline(sketch, "E185", {"points": [v(494.18, 24.49) * mm, v(494.18, 22.08) * mm, v(493.26, 17.48) * mm, v(492.14, 14.26) * mm]});
            skFitSpline(sketch, "E186", {"points": [v(492.14, 14.26) * mm, v(490.1, 8.41) * mm, v(490.07, 8.4) * mm, v(476.53, 8.4) * mm]});
            skFitSpline(sketch, "E187", {"points": [v(476.53, 8.4) * mm, v(466.58, 8.4) * mm, v(462.7, 7.7) * mm, v(461.96, 5.79) * mm]});
            skFitSpline(sketch, "E188", {"points": [v(461.96, 5.79) * mm, v(461.4, 4.35) * mm, v(459.93, -6.74) * mm, v(458.69, -18.85) * mm]});
            skFitSpline(sketch, "E189", {"points": [v(458.69, -18.85) * mm, v(456.19, -43.13) * mm, v(457.42, -58.1) * mm, v(462.05, -59.89) * mm]});
            skFitSpline(sketch, "E190", {"points": [v(462.05, -59.89) * mm, v(466.54, -61.6) * mm, v(480.7, -53.25) * mm, v(493.44, -41.34) * mm]});
            skFitSpline(sketch, "E191", {"points": [v(493.44, -41.34) * mm, v(499.73, -35.46) * mm, v(505.73, -30.65) * mm, v(506.77, -30.65) * mm]});
            skFitSpline(sketch, "E192", {"points": [v(506.77, -30.65) * mm, v(510.1, -30.65) * mm, v(511.02, -39.58) * mm, v(508.46, -47.01) * mm]});
            skFitSpline(sketch, "E193", {"points": [v(508.46, -47.01) * mm, v(500.27, -70.78) * mm, v(464.23, -93.67) * mm, v(443.63, -88.18) * mm]});
            skFitSpline(sketch, "E194", {"points": [v(443.63, -88.18) * mm, v(436.32, -86.23) * mm, v(430.49, -78.96) * mm, v(428.05, -68.77) * mm]});
            skFitSpline(sketch, "E195", {"points": [v(428.05, -68.77) * mm, v(426, -60.18) * mm, v(425.55, -59.99) * mm, v(418.25, -64.52) * mm]});
            skFitSpline(sketch, "E196", {"points": [v(418.25, -64.52) * mm, v(412.67, -68) * mm, v(408.97, -68.73) * mm, v(397.88, -68.57) * mm]});
            skFitSpline(sketch, "E197", {"points": [v(397.88, -68.57) * mm, v(384.98, -68.4) * mm, v(384.01, -68.68) * mm, v(377.5, -74.64) * mm]});
            skFitSpline(sketch, "E198", {"points": [v(377.5, -74.64) * mm, v(365.8, -85.37) * mm, v(355.8, -89.15) * mm, v(337.98, -89.6) * mm]});
            skFitSpline(sketch, "E199", {"points": [v(337.98, -89.6) * mm, v(329.28, -89.82) * mm, v(320.07, -89.33) * mm, v(317.5, -88.5) * mm]});
            skFitSpline(sketch, "E200", {"points": [v(385.7, -25.43) * mm, v(386.64, -17.46) * mm, v(386.3, -15.64) * mm, v(383.66, -14.63) * mm]});
            skFitSpline(sketch, "E201", {"points": [v(383.66, -14.63) * mm, v(379.08, -12.87) * mm, v(376.38, -16.52) * mm, v(376.67, -24.09) * mm]});
            skFitSpline(sketch, "E202", {"points": [v(376.67, -24.09) * mm, v(376.97, -32.15) * mm, v(380.4, -39.18) * mm, v(382.83, -36.75) * mm]});
            skFitSpline(sketch, "E203", {"points": [v(382.83, -36.75) * mm, v(383.78, -35.8) * mm, v(385.07, -30.7) * mm, v(385.7, -25.43) * mm]});
            skFitSpline(sketch, "E204", {"points": [v(-539.73, 126.1) * mm, v(-551.06, 131.84) * mm, v(-551, 146.27) * mm, v(-539.62, 152.05) * mm]});
            skFitSpline(sketch, "E205", {"points": [v(-539.62, 152.05) * mm, v(-533.86, 154.98) * mm, v(-526.13, 155.3) * mm, v(-462.1, 155.3) * mm]});
            skLineSegment(sketch, "E206", {"start": v(-462.1, 155.3) * mm, "end": v(-390.97, 155.3) * mm});
            skLineSegment(sketch, "E207", {"start": v(-390.97, 155.3) * mm, "end": v(-390.97, 160.85) * mm});
            skFitSpline(sketch, "E208", {"points": [v(-390.97, 160.85) * mm, v(-390.97, 170.05) * mm, v(-385.48, 181.2) * mm, v(-379.4, 184.35) * mm]});
            skFitSpline(sketch, "E209", {"points": [v(-379.4, 184.35) * mm, v(-373.17, 187.57) * mm, v(-10.28, 250.15) * mm, v(2.18, 250.15) * mm]});
            skFitSpline(sketch, "E210", {"points": [v(2.18, 250.15) * mm, v(10.33, 250.15) * mm, v(362.94, 190.41) * mm, v(375.5, 186.9) * mm]});
            skFitSpline(sketch, "E211", {"points": [v(375.5, 186.9) * mm, v(384.93, 184.27) * mm, v(391.52, 175.86) * mm, v(393.02, 164.53) * mm]});
            skLineSegment(sketch, "E212", {"start": v(393.02, 164.53) * mm, "end": v(394.24, 155.3) * mm});
            skLineSegment(sketch, "E213", {"start": v(394.24, 155.3) * mm, "end": v(464.39, 155.3) * mm});
            skFitSpline(sketch, "E214", {"points": [v(464.39, 155.3) * mm, v(536.67, 155.3) * mm, v(544.5, 154.6) * mm, v(548.14, 147.8) * mm]});
            skFitSpline(sketch, "E215", {"points": [v(548.14, 147.8) * mm, v(551.05, 142.36) * mm, v(550.26, 133.77) * mm, v(546.41, 129.02) * mm]});
            skLineSegment(sketch, "E216", {"start": v(546.41, 129.02) * mm, "end": v(542.86, 124.63) * mm});
            skLineSegment(sketch, "E217", {"start": v(542.86, 124.63) * mm, "end": v(3.88, 124.18) * mm});
            skFitSpline(sketch, "E218", {"points": [v(3.88, 124.18) * mm, v(-428.24, 123.83) * mm, v(-536, 124.2) * mm, v(-539.73, 126.1) * mm]});
            skLineSegment(sketch, "E219", {"start": v(-539.73, 126.1) * mm, "end": v(-539.73, 126.1) * mm});
            skSolve(sketch);
        }
        {
            var Q0;
            Q0=makeQuery(id+"F3.opExtrude","CAP_FACE",FACE,{"disambiguationData":[OSD([sQuery(id+"F2.wireOp",EDGE,"E1.bottom"),sQuery(id+"F2.wireOp",EDGE,"E1.top"),sQuery(id+"F2.wireOp",EDGE,"E1.left"),sQuery(id+"F2.wireOp",EDGE,"E1.right")])],"isStart":false});
            var sketch = newSketch(context, id + "F7", { "sketchPlane" : qUnion([Q0])});
            skFitSpline(sketch, "E220", {"points": [v(-4.02, 72.8) * mm, v(-5.86, 73.18) * mm, v(-39.6, 78.99) * mm, v(-78.98, 85.71) * mm]});
            skFitSpline(sketch, "E221", {"points": [v(-78.98, 85.71) * mm, v(-121.51, 92.97) * mm, v(-151.23, 98.37) * mm, v(-152.13, 99) * mm]});
            skFitSpline(sketch, "E222", {"points": [v(-152.13, 99) * mm, v(-154.65, 100.77) * mm, v(-155.8, 102.96) * mm, v(-156.27, 106.9) * mm]});
            skLineSegment(sketch, "E223", {"start": v(-156.27, 106.9) * mm, "end": v(-156.7, 110.63) * mm});
            skLineSegment(sketch, "E224", {"start": v(-156.7, 110.63) * mm, "end": v(-185.43, 110.64) * mm});
            skFitSpline(sketch, "E225", {"points": [v(-185.43, 110.64) * mm, v(-216.4, 110.65) * mm, v(-217, 110.72) * mm, v(-218.85, 114.58) * mm]});
            skFitSpline(sketch, "E226", {"points": [v(-218.85, 114.58) * mm, v(-220.24, 117.49) * mm, v(-219.12, 120.37) * mm, v(-215.96, 121.97) * mm]});
            skFitSpline(sketch, "E227", {"points": [v(-215.96, 121.97) * mm, v(-213.54, 123.2) * mm, v(-201.69, 123.27) * mm, v(0.15, 123.27) * mm]});
            skFitSpline(sketch, "E228", {"points": [v(0.15, 123.27) * mm, v(154.15, 123.27) * mm, v(214.36, 123.04) * mm, v(216.06, 122.45) * mm]});
            skFitSpline(sketch, "E229", {"points": [v(216.06, 122.45) * mm, v(217.36, 122) * mm, v(218.75, 121.02) * mm, v(219.15, 120.27) * mm]});
            skFitSpline(sketch, "E230", {"points": [v(219.15, 120.27) * mm, v(220.3, 118.1) * mm, v(220, 114.66) * mm, v(218.45, 112.76) * mm]});
            skLineSegment(sketch, "E231", {"start": v(218.45, 112.76) * mm, "end": v(217.03, 111) * mm});
            skLineSegment(sketch, "E232", {"start": v(217.03, 111) * mm, "end": v(187.03, 110.63) * mm});
            skLineSegment(sketch, "E233", {"start": v(187.03, 110.63) * mm, "end": v(157.02, 110.26) * mm});
            skLineSegment(sketch, "E234", {"start": v(157.02, 110.26) * mm, "end": v(156.89, 107.16) * mm});
            skFitSpline(sketch, "E235", {"points": [v(156.89, 107.16) * mm, v(156.68, 102.47) * mm, v(154.96, 99.8) * mm, v(151.27, 98.44) * mm]});
            skFitSpline(sketch, "E236", {"points": [v(151.27, 98.44) * mm, v(148.68, 97.48) * mm, v(0.92, 71.75) * mm, v(-0.3, 72.04) * mm]});
            skFitSpline(sketch, "E237", {"points": [v(-0.3, 72.04) * mm, v(-0.5, 72.09) * mm, v(-2.18, 72.43) * mm, v(-4.02, 72.8) * mm]});
            skLineSegment(sketch, "E238", {"start": v(-4.02, 72.8) * mm, "end": v(-4.02, 72.8) * mm});
            skFitSpline(sketch, "E239", {"points": [v(65.16, 135.44) * mm, v(57.71, 137.18) * mm, v(51.02, 139.75) * mm, v(47.2, 142.32) * mm]});
            skLineSegment(sketch, "E240", {"start": v(47.2, 142.32) * mm, "end": v(43.41, 144.86) * mm});
            skLineSegment(sketch, "E241", {"start": v(43.41, 144.86) * mm, "end": v(40.57, 142.3) * mm});
            skFitSpline(sketch, "E242", {"points": [v(40.57, 142.3) * mm, v(37.06, 139.12) * mm, v(34.31, 137.67) * mm, v(29.98, 136.7) * mm]});
            skFitSpline(sketch, "E243", {"points": [v(29.98, 136.7) * mm, v(21.03, 134.7) * mm, v(17.62, 141.67) * mm, v(20.1, 156.92) * mm]});
            skFitSpline(sketch, "E244", {"points": [v(20.1, 156.92) * mm, v(21.74, 167.04) * mm, v(21.67, 168.5) * mm, v(19.44, 169.51) * mm]});
            skFitSpline(sketch, "E245", {"points": [v(19.44, 169.51) * mm, v(16.97, 170.64) * mm, v(14.54, 169) * mm, v(11.84, 164.39) * mm]});
            skFitSpline(sketch, "E246", {"points": [v(11.84, 164.39) * mm, v(8.3, 158.34) * mm, v(7.26, 154.32) * mm, v(8.1, 149.86) * mm]});
            skFitSpline(sketch, "E247", {"points": [v(8.1, 149.86) * mm, v(8.5, 147.71) * mm, v(8.87, 144.64) * mm, v(8.92, 143.03) * mm]});
            skFitSpline(sketch, "E248", {"points": [v(8.92, 143.03) * mm, v(9, 140.4) * mm, v(8.69, 139.88) * mm, v(5.87, 137.89) * mm]});
            skFitSpline(sketch, "E249", {"points": [v(5.87, 137.89) * mm, v(1.64, 134.9) * mm, v(-3.13, 134.68) * mm, v(-4.53, 137.4) * mm]});
            skFitSpline(sketch, "E250", {"points": [v(-4.53, 137.4) * mm, v(-5.7, 139.68) * mm, v(-5.78, 149.47) * mm, v(-4.73, 161.2) * mm]});
            skFitSpline(sketch, "E251", {"points": [v(-4.73, 161.2) * mm, v(-3.79, 171.71) * mm, v(-4.05, 173.1) * mm, v(-6.94, 173.1) * mm]});
            skFitSpline(sketch, "E252", {"points": [v(-6.94, 173.1) * mm, v(-9.67, 173.1) * mm, v(-12.3, 170.1) * mm, v(-15.66, 163.09) * mm]});
            skFitSpline(sketch, "E253", {"points": [v(-15.66, 163.09) * mm, v(-18.48, 157.2) * mm, v(-18.76, 153.85) * mm, v(-17.02, 146.47) * mm]});
            skFitSpline(sketch, "E254", {"points": [v(-17.02, 146.47) * mm, v(-15.68, 140.78) * mm, v(-16.07, 139.86) * mm, v(-20.99, 137.18) * mm]});
            skFitSpline(sketch, "E255", {"points": [v(-20.99, 137.18) * mm, v(-27.42, 133.68) * mm, v(-30.19, 134.83) * mm, v(-31.13, 141.4) * mm]});
            skLineSegment(sketch, "E256", {"start": v(-31.13, 141.4) * mm, "end": v(-31.66, 145.04) * mm});
            skLineSegment(sketch, "E257", {"start": v(-31.66, 145.04) * mm, "end": v(-34.76, 142.05) * mm});
            skFitSpline(sketch, "E258", {"points": [v(-34.76, 142.05) * mm, v(-38.93, 138.02) * mm, v(-42.08, 136.56) * mm, v(-46.82, 136.45) * mm]});
            skFitSpline(sketch, "E259", {"points": [v(-46.82, 136.45) * mm, v(-51.45, 136.34) * mm, v(-53.29, 137.58) * mm, v(-55.43, 142.24) * mm]});
            skFitSpline(sketch, "E260", {"points": [v(-55.43, 142.24) * mm, v(-57.76, 147.32) * mm, v(-56.74, 159.36) * mm, v(-53.44, 165.75) * mm]});
            skLineSegment(sketch, "E261", {"start": v(-53.44, 165.75) * mm, "end": v(-52.29, 167.98) * mm});
            skLineSegment(sketch, "E262", {"start": v(-52.29, 167.98) * mm, "end": v(-56.59, 167.76) * mm});
            skLineSegment(sketch, "E263", {"start": v(-56.59, 167.76) * mm, "end": v(-60.89, 167.53) * mm});
            skLineSegment(sketch, "E264", {"start": v(-60.89, 167.53) * mm, "end": v(-62.25, 161.95) * mm});
            skFitSpline(sketch, "E265", {"points": [v(-62.25, 161.95) * mm, v(-63.3, 157.62) * mm, v(-63.52, 154.56) * mm, v(-63.24, 148.25) * mm]});
            skFitSpline(sketch, "E266", {"points": [v(-63.24, 148.25) * mm, v(-63.03, 143.64) * mm, v(-63.18, 139.53) * mm, v(-63.59, 138.77) * mm]});
            skFitSpline(sketch, "E267", {"points": [v(-63.59, 138.77) * mm, v(-64.61, 136.85) * mm, v(-68.2, 135.17) * mm, v(-71.28, 135.17) * mm]});
            skFitSpline(sketch, "E268", {"points": [v(-71.28, 135.17) * mm, v(-74.54, 135.17) * mm, v(-75.88, 137) * mm, v(-76.6, 142.43) * mm]});
            skLineSegment(sketch, "E269", {"start": v(-76.6, 142.43) * mm, "end": v(-77.1, 146.34) * mm});
            skLineSegment(sketch, "E270", {"start": v(-77.1, 146.34) * mm, "end": v(-80.28, 143.42) * mm});
            skFitSpline(sketch, "E271", {"points": [v(-80.28, 143.42) * mm, v(-84.07, 139.93) * mm, v(-88.18, 137.72) * mm, v(-92.86, 136.67) * mm]});
            skFitSpline(sketch, "E272", {"points": [v(-92.86, 136.67) * mm, v(-97.59, 135.61) * mm, v(-100.15, 136.99) * mm, v(-101.87, 141.51) * mm]});
            skLineSegment(sketch, "E273", {"start": v(-101.87, 141.51) * mm, "end": v(-103.17, 144.9) * mm});
            skLineSegment(sketch, "E274", {"start": v(-103.17, 144.9) * mm, "end": v(-105.29, 142.34) * mm});
            skFitSpline(sketch, "E275", {"points": [v(-105.29, 142.34) * mm, v(-111.87, 134.36) * mm, v(-126.66, 133.64) * mm, v(-132.85, 141) * mm]});
            skFitSpline(sketch, "E276", {"points": [v(-132.85, 141) * mm, v(-135.78, 144.48) * mm, v(-136.68, 148.03) * mm, v(-136.17, 154.08) * mm]});
            skFitSpline(sketch, "E277", {"points": [v(-136.17, 154.08) * mm, v(-135.36, 163.6) * mm, v(-131.77, 171.23) * mm, v(-125.36, 177.03) * mm]});
            skFitSpline(sketch, "E278", {"points": [v(-125.36, 177.03) * mm, v(-119.29, 182.5) * mm, v(-110.9, 185.05) * mm, v(-104, 183.5) * mm]});
            skFitSpline(sketch, "E279", {"points": [v(-104, 183.5) * mm, v(-101.13, 182.87) * mm, v(-100.3, 182.93) * mm, v(-99.25, 183.87) * mm]});
            skFitSpline(sketch, "E280", {"points": [v(-99.25, 183.87) * mm, v(-96.48, 186.38) * mm, v(-90.9, 184.1) * mm, v(-88.4, 179.46) * mm]});
            skLineSegment(sketch, "E281", {"start": v(-88.4, 179.46) * mm, "end": v(-87, 176.85) * mm});
            skLineSegment(sketch, "E282", {"start": v(-87, 176.85) * mm, "end": v(-89.4, 171.99) * mm});
            skFitSpline(sketch, "E283", {"points": [v(-89.4, 171.99) * mm, v(-91.68, 167.35) * mm, v(-91.79, 166.74) * mm, v(-91.78, 158.4) * mm]});
            skFitSpline(sketch, "E284", {"points": [v(-91.78, 158.4) * mm, v(-91.76, 148.82) * mm, v(-91.35, 147.39) * mm, v(-88.84, 148.18) * mm]});
            skFitSpline(sketch, "E285", {"points": [v(-88.84, 148.18) * mm, v(-86.14, 149.04) * mm, v(-75.42, 159.87) * mm, v(-75.42, 161.74) * mm]});
            skFitSpline(sketch, "E286", {"points": [v(-75.42, 161.74) * mm, v(-75.42, 162.64) * mm, v(-74.6, 165.64) * mm, v(-73.6, 168.41) * mm]});
            skFitSpline(sketch, "E287", {"points": [v(-73.6, 168.41) * mm, v(-71.82, 173.31) * mm, v(-71.8, 173.5) * mm, v(-73.13, 174.95) * mm]});
            skFitSpline(sketch, "E288", {"points": [v(-73.13, 174.95) * mm, v(-75.5, 177.57) * mm, v(-76.32, 179.85) * mm, v(-75.83, 182.46) * mm]});
            skFitSpline(sketch, "E289", {"points": [v(-75.83, 182.46) * mm, v(-75.24, 185.64) * mm, v(-72.96, 187.24) * mm, v(-69.04, 187.24) * mm]});
            skFitSpline(sketch, "E290", {"points": [v(-69.04, 187.24) * mm, v(-65.37, 187.24) * mm, v(-62.6, 184.92) * mm, v(-60.4, 180) * mm]});
            skFitSpline(sketch, "E291", {"points": [v(-60.4, 180) * mm, v(-59.19, 177.28) * mm, v(-58.67, 176.83) * mm, v(-56.73, 176.83) * mm]});
            skFitSpline(sketch, "E292", {"points": [v(-56.73, 176.83) * mm, v(-55.5, 176.83) * mm, v(-52.27, 177.71) * mm, v(-49.58, 178.8) * mm]});
            skFitSpline(sketch, "E293", {"points": [v(-49.58, 178.8) * mm, v(-43.83, 181.09) * mm, v(-43.08, 180.85) * mm, v(-40.6, 175.9) * mm]});
            skLineSegment(sketch, "E294", {"start": v(-40.6, 175.9) * mm, "end": v(-38.86, 172.45) * mm});
            skLineSegment(sketch, "E295", {"start": v(-38.86, 172.45) * mm, "end": v(-41.95, 161.2) * mm});
            skFitSpline(sketch, "E296", {"points": [v(-41.95, 161.2) * mm, v(-46.22, 145.7) * mm, v(-45.52, 144.63) * mm, v(-36.56, 153) * mm]});
            skLineSegment(sketch, "E297", {"start": v(-36.56, 153) * mm, "end": v(-31.01, 158.17) * mm});
            skLineSegment(sketch, "E298", {"start": v(-31.01, 158.17) * mm, "end": v(-30.57, 162.9) * mm});
            skFitSpline(sketch, "E299", {"points": [v(-30.57, 162.9) * mm, v(-30.02, 168.87) * mm, v(-27.58, 176.33) * mm, v(-24.53, 181.43) * mm]});
            skFitSpline(sketch, "E300", {"points": [v(-24.53, 181.43) * mm, v(-22.6, 184.65) * mm, v(-21.74, 185.42) * mm, v(-19.9, 185.6) * mm]});
            skFitSpline(sketch, "E301", {"points": [v(-19.9, 185.6) * mm, v(-18.1, 185.79) * mm, v(-17.17, 185.3) * mm, v(-15.37, 183.26) * mm]});
            skFitSpline(sketch, "E302", {"points": [v(-15.37, 183.26) * mm, v(-14.13, 181.85) * mm, v(-12.97, 180.27) * mm, v(-12.8, 179.76) * mm]});
            skFitSpline(sketch, "E303", {"points": [v(-12.8, 179.76) * mm, v(-12.6, 179.14) * mm, v(-11.46, 179.59) * mm, v(-9.31, 181.14) * mm]});
            skFitSpline(sketch, "E304", {"points": [v(-9.31, 181.14) * mm, v(-4.9, 184.34) * mm, v(-0.58, 184.9) * mm, v(3.7, 182.82) * mm]});
            skFitSpline(sketch, "E305", {"points": [v(3.7, 182.82) * mm, v(7.18, 181.14) * mm, v(8.97, 179.06) * mm, v(9.8, 175.74) * mm]});
            skLineSegment(sketch, "E306", {"start": v(9.8, 175.74) * mm, "end": v(10.3, 173.75) * mm});
            skLineSegment(sketch, "E307", {"start": v(10.3, 173.75) * mm, "end": v(12.25, 175.62) * mm});
            skFitSpline(sketch, "E308", {"points": [v(12.25, 175.62) * mm, v(17.33, 180.47) * mm, v(26.31, 182.02) * mm, v(31, 178.85) * mm]});
            skFitSpline(sketch, "E309", {"points": [v(31, 178.85) * mm, v(32.4, 177.92) * mm, v(33.94, 176.33) * mm, v(34.45, 175.32) * mm]});
            skFitSpline(sketch, "E310", {"points": [v(34.45, 175.32) * mm, v(35.9, 172.45) * mm, v(35.57, 166) * mm, v(33.55, 157.63) * mm]});
            skFitSpline(sketch, "E311", {"points": [v(33.55, 157.63) * mm, v(32.52, 153.4) * mm, v(31.69, 149.48) * mm, v(31.69, 148.89) * mm]});
            skFitSpline(sketch, "E312", {"points": [v(31.69, 148.89) * mm, v(31.69, 146.54) * mm, v(34.4, 148.1) * mm, v(40.28, 153.85) * mm]});
            skFitSpline(sketch, "E313", {"points": [v(40.28, 153.85) * mm, v(44.14, 157.62) * mm, v(46.79, 159.67) * mm, v(47.35, 159.33) * mm]});
            skFitSpline(sketch, "E314", {"points": [v(47.35, 159.33) * mm, v(47.95, 158.95) * mm, v(48.11, 157.38) * mm, v(47.84, 154.41) * mm]});
            skFitSpline(sketch, "E315", {"points": [v(47.84, 154.41) * mm, v(47.47, 150.27) * mm, v(47.53, 150.05) * mm, v(49.13, 150.05) * mm]});
            skFitSpline(sketch, "E316", {"points": [v(49.13, 150.05) * mm, v(50.7, 150.05) * mm, v(50.83, 150.44) * mm, v(51.25, 156.19) * mm]});
            skFitSpline(sketch, "E317", {"points": [v(51.25, 156.19) * mm, v(52.17, 169.14) * mm, v(59.1, 189.49) * mm, v(64.13, 194.01) * mm]});
            skFitSpline(sketch, "E318", {"points": [v(64.13, 194.01) * mm, v(71.1, 200.3) * mm, v(71.85, 195.23) * mm, v(67.26, 173.1) * mm]});
            skFitSpline(sketch, "E319", {"points": [v(67.26, 173.1) * mm, v(65.38, 164.06) * mm, v(63.36, 146.58) * mm, v(64.09, 145.7) * mm]});
            skFitSpline(sketch, "E320", {"points": [v(64.09, 145.7) * mm, v(64.6, 145.1) * mm, v(70.27, 144.14) * mm, v(73.34, 144.12) * mm]});
            skFitSpline(sketch, "E321", {"points": [v(73.34, 144.12) * mm, v(80.28, 144.1) * mm, v(86.16, 147.32) * mm, v(88.22, 152.3) * mm]});
            skFitSpline(sketch, "E322", {"points": [v(88.22, 152.3) * mm, v(89.7, 155.84) * mm, v(88.86, 165.57) * mm, v(86.8, 168.9) * mm]});
            skFitSpline(sketch, "E323", {"points": [v(86.8, 168.9) * mm, v(85.14, 171.6) * mm, v(85.07, 171.62) * mm, v(80.14, 171.62) * mm]});
            skFitSpline(sketch, "E324", {"points": [v(80.14, 171.62) * mm, v(74.8, 171.62) * mm, v(72.33, 172.7) * mm, v(71.64, 175.32) * mm]});
            skFitSpline(sketch, "E325", {"points": [v(71.64, 175.32) * mm, v(71.42, 176.18) * mm, v(71.81, 177.53) * mm, v(72.57, 178.46) * mm]});
            skFitSpline(sketch, "E326", {"points": [v(72.57, 178.46) * mm, v(73.65, 179.8) * mm, v(74.91, 180.16) * mm, v(79.74, 180.5) * mm]});
            skFitSpline(sketch, "E327", {"points": [v(79.74, 180.5) * mm, v(85.34, 180.9) * mm, v(85.65, 181.02) * mm, v(86.7, 183.15) * mm]});
            skFitSpline(sketch, "E328", {"points": [v(86.7, 183.15) * mm, v(87.3, 184.38) * mm, v(87.8, 187.4) * mm, v(87.8, 189.85) * mm]});
            skFitSpline(sketch, "E329", {"points": [v(87.8, 189.85) * mm, v(87.81, 197.65) * mm, v(84.36, 200.65) * mm, v(74.71, 201.22) * mm]});
            skFitSpline(sketch, "E330", {"points": [v(74.71, 201.22) * mm, v(67.9, 201.62) * mm, v(62.96, 200.56) * mm, v(55.88, 197.17) * mm]});
            skFitSpline(sketch, "E331", {"points": [v(55.88, 197.17) * mm, v(49.82, 194.26) * mm, v(47.3, 193.97) * mm, v(47.3, 196.18) * mm]});
            skFitSpline(sketch, "E332", {"points": [v(47.3, 196.18) * mm, v(47.3, 200.18) * mm, v(57.13, 207.33) * mm, v(66.24, 209.96) * mm]});
            skFitSpline(sketch, "E333", {"points": [v(66.24, 209.96) * mm, v(72.35, 211.72) * mm, v(84.52, 211.15) * mm, v(90.82, 208.8) * mm]});
            skFitSpline(sketch, "E334", {"points": [v(90.82, 208.8) * mm, v(96.65, 206.62) * mm, v(101.76, 201.55) * mm, v(102.97, 196.71) * mm]});
            skFitSpline(sketch, "E335", {"points": [v(102.97, 196.71) * mm, v(104.88, 189.14) * mm, v(103.62, 184.53) * mm, v(98.2, 179.25) * mm]});
            skFitSpline(sketch, "E336", {"points": [v(98.2, 179.25) * mm, v(96, 177.1) * mm, v(94.48, 175.34) * mm, v(94.82, 175.34) * mm]});
            skFitSpline(sketch, "E337", {"points": [v(94.82, 175.34) * mm, v(96.3, 175.34) * mm, v(102.36, 169.1) * mm, v(103.81, 166.1) * mm]});
            skFitSpline(sketch, "E338", {"points": [v(103.81, 166.1) * mm, v(106.07, 161.42) * mm, v(106.16, 152.36) * mm, v(103.99, 148.1) * mm]});
            skFitSpline(sketch, "E339", {"points": [v(103.99, 148.1) * mm, v(101.64, 143.52) * mm, v(95.7, 138.56) * mm, v(90.26, 136.67) * mm]});
            skFitSpline(sketch, "E340", {"points": [v(90.26, 136.67) * mm, v(84.46, 134.65) * mm, v(71.3, 134) * mm, v(65.16, 135.44) * mm]});
            skFitSpline(sketch, "E341", {"points": [v(-112.85, 147.12) * mm, v(-107.25, 149.24) * mm, v(-103.73, 155.26) * mm, v(-103.7, 162.75) * mm]});
            skFitSpline(sketch, "E342", {"points": [v(-103.7, 162.75) * mm, v(-103.7, 165.43) * mm, v(-103.33, 169.57) * mm, v(-102.9, 171.93) * mm]});
            skFitSpline(sketch, "E343", {"points": [v(-102.9, 171.93) * mm, v(-102.46, 174.3) * mm, v(-102.28, 176.41) * mm, v(-102.5, 176.64) * mm]});
            skFitSpline(sketch, "E344", {"points": [v(-102.5, 176.64) * mm, v(-103.28, 177.42) * mm, v(-109.7, 174.44) * mm, v(-113.2, 171.68) * mm]});
            skFitSpline(sketch, "E345", {"points": [v(-113.2, 171.68) * mm, v(-118.2, 167.72) * mm, v(-120.95, 162.32) * mm, v(-121.38, 155.55) * mm]});
            skFitSpline(sketch, "E346", {"points": [v(-121.38, 155.55) * mm, v(-121.7, 150.53) * mm, v(-121.6, 150.04) * mm, v(-119.8, 148.25) * mm]});
            skFitSpline(sketch, "E347", {"points": [v(-119.8, 148.25) * mm, v(-117.72, 146.17) * mm, v(-116.09, 145.9) * mm, v(-112.85, 147.12) * mm]});
            skFitSpline(sketch, "E348", {"points": [v(-183.84, 136) * mm, v(-185.9, 138.13) * mm, v(-184.4, 157.8) * mm, v(-181.44, 167.09) * mm]});
            skFitSpline(sketch, "E349", {"points": [v(-181.44, 167.09) * mm, v(-180.97, 168.57) * mm, v(-181.2, 168.65) * mm, v(-186.2, 168.65) * mm]});
            skFitSpline(sketch, "E350", {"points": [v(-186.2, 168.65) * mm, v(-190.78, 168.65) * mm, v(-191.46, 168.82) * mm, v(-191.46, 170) * mm]});
            skFitSpline(sketch, "E351", {"points": [v(-191.46, 170) * mm, v(-191.46, 172.08) * mm, v(-187.7, 175.19) * mm, v(-182.96, 177.03) * mm]});
            skLineSegment(sketch, "E352", {"start": v(-182.96, 177.03) * mm, "end": v(-178.64, 178.7) * mm});
            skLineSegment(sketch, "E353", {"start": v(-178.64, 178.7) * mm, "end": v(-175.48, 187.62) * mm});
            skFitSpline(sketch, "E354", {"points": [v(-175.48, 187.62) * mm, v(-173.75, 192.53) * mm, v(-172.06, 197.16) * mm, v(-171.74, 197.93) * mm]});
            skFitSpline(sketch, "E355", {"points": [v(-171.74, 197.93) * mm, v(-171.2, 199.2) * mm, v(-171.42, 199.27) * mm, v(-174.43, 198.78) * mm]});
            skFitSpline(sketch, "E356", {"points": [v(-174.43, 198.78) * mm, v(-179.3, 198) * mm, v(-183.51, 195.92) * mm, v(-187.21, 192.52) * mm]});
            skFitSpline(sketch, "E357", {"points": [v(-187.21, 192.52) * mm, v(-191.98, 188.12) * mm, v(-193.7, 188.58) * mm, v(-193.7, 194.26) * mm]});
            skFitSpline(sketch, "E358", {"points": [v(-193.7, 194.26) * mm, v(-193.7, 199.51) * mm, v(-187.2, 205.3) * mm, v(-178.22, 208.08) * mm]});
            skFitSpline(sketch, "E359", {"points": [v(-178.22, 208.08) * mm, v(-170.95, 210.33) * mm, v(-162.53, 210.91) * mm, v(-143.6, 210.48) * mm]});
            skFitSpline(sketch, "E360", {"points": [v(-143.6, 210.48) * mm, v(-124.58, 210.05) * mm, v(-124.9, 210.15) * mm, v(-127.15, 204.87) * mm]});
            skFitSpline(sketch, "E361", {"points": [v(-127.15, 204.87) * mm, v(-129.57, 199.2) * mm, v(-129.71, 199.15) * mm, v(-144.5, 199.13) * mm]});
            skLineSegment(sketch, "E362", {"start": v(-144.5, 199.13) * mm, "end": v(-157.62, 199.12) * mm});
            skLineSegment(sketch, "E363", {"start": v(-157.62, 199.12) * mm, "end": v(-159.58, 191.14) * mm});
            skFitSpline(sketch, "E364", {"points": [v(-159.58, 191.14) * mm, v(-160.65, 186.74) * mm, v(-161.66, 182.65) * mm, v(-161.8, 182.04) * mm]});
            skFitSpline(sketch, "E365", {"points": [v(-161.8, 182.04) * mm, v(-162.04, 181.1) * mm, v(-160.6, 180.89) * mm, v(-152.8, 180.7) * mm]});
            skFitSpline(sketch, "E366", {"points": [v(-152.8, 180.7) * mm, v(-146.97, 180.58) * mm, v(-143.35, 180.2) * mm, v(-143.02, 179.66) * mm]});
            skFitSpline(sketch, "E367", {"points": [v(-143.02, 179.66) * mm, v(-142.41, 178.68) * mm, v(-144.07, 172.79) * mm, v(-145.4, 171.17) * mm]});
            skFitSpline(sketch, "E368", {"points": [v(-145.4, 171.17) * mm, v(-146.2, 170.23) * mm, v(-147.83, 170.13) * mm, v(-155.74, 170.56) * mm]});
            skLineSegment(sketch, "E369", {"start": v(-155.74, 170.56) * mm, "end": v(-165.13, 171.07) * mm});
            skLineSegment(sketch, "E370", {"start": v(-165.13, 171.07) * mm, "end": v(-166.72, 164.47) * mm});
            skFitSpline(sketch, "E371", {"points": [v(-166.72, 164.47) * mm, v(-168.53, 156.92) * mm, v(-169.62, 150.4) * mm, v(-170.3, 143.15) * mm]});
            skFitSpline(sketch, "E372", {"points": [v(-170.3, 143.15) * mm, v(-170.69, 138.84) * mm, v(-171.03, 137.92) * mm, v(-172.64, 136.87) * mm]});
            skFitSpline(sketch, "E373", {"points": [v(-172.64, 136.87) * mm, v(-175.08, 135.27) * mm, v(-182.56, 134.7) * mm, v(-183.84, 136) * mm]});
            skFitSpline(sketch, "E374", {"points": [v(126.9, 136.58) * mm, v(121.05, 138.46) * mm, v(115.7, 143.46) * mm, v(114.21, 148.4) * mm]});
            skFitSpline(sketch, "E375", {"points": [v(114.21, 148.4) * mm, v(112.76, 153.26) * mm, v(113.59, 163.12) * mm, v(115.87, 168.03) * mm]});
            skFitSpline(sketch, "E376", {"points": [v(115.87, 168.03) * mm, v(119.6, 176.03) * mm, v(126.32, 181.7) * mm, v(134.25, 183.54) * mm]});
            skFitSpline(sketch, "E377", {"points": [v(134.25, 183.54) * mm, v(141.52, 185.22) * mm, v(151.26, 183.23) * mm, v(154.42, 179.43) * mm]});
            skFitSpline(sketch, "E378", {"points": [v(154.42, 179.43) * mm, v(155.9, 177.65) * mm, v(154.6, 177.1) * mm, v(147.83, 176.64) * mm]});
            skFitSpline(sketch, "E379", {"points": [v(147.83, 176.64) * mm, v(144.69, 176.43) * mm, v(140.93, 175.75) * mm, v(139.47, 175.14) * mm]});
            skFitSpline(sketch, "E380", {"points": [v(139.47, 175.14) * mm, v(132.67, 172.3) * mm, v(128.2, 165.5) * mm, v(128.1, 157.86) * mm]});
            skFitSpline(sketch, "E381", {"points": [v(128.1, 157.86) * mm, v(127.97, 148.8) * mm, v(133.7, 144.61) * mm, v(142.75, 147.13) * mm]});
            skLineSegment(sketch, "E382", {"start": v(142.75, 147.13) * mm, "end": v(145.58, 147.91) * mm});
            skLineSegment(sketch, "E383", {"start": v(145.58, 147.91) * mm, "end": v(143.02, 150.75) * mm});
            skFitSpline(sketch, "E384", {"points": [v(143.02, 150.75) * mm, v(134.47, 160.22) * mm, v(139.5, 174.6) * mm, v(151.37, 174.6) * mm]});
            skFitSpline(sketch, "E385", {"points": [v(151.37, 174.6) * mm, v(155.58, 174.6) * mm, v(157.91, 173.5) * mm, v(159.66, 170.71) * mm]});
            skFitSpline(sketch, "E386", {"points": [v(159.66, 170.71) * mm, v(160.95, 168.66) * mm, v(161.14, 167.4) * mm, v(160.87, 162.7) * mm]});
            skFitSpline(sketch, "E387", {"points": [v(160.87, 162.7) * mm, v(160.69, 159.63) * mm, v(160.3, 156.36) * mm, v(160, 155.44) * mm]});
            skFitSpline(sketch, "E388", {"points": [v(160, 155.44) * mm, v(159.32, 153.37) * mm, v(160.82, 153.21) * mm, v(164.31, 154.97) * mm]});
            skFitSpline(sketch, "E389", {"points": [v(164.31, 154.97) * mm, v(168.41, 157.05) * mm, v(170.04, 159) * mm, v(170.07, 161.9) * mm]});
            skFitSpline(sketch, "E390", {"points": [v(170.07, 161.9) * mm, v(170.08, 163.36) * mm, v(170.53, 166.81) * mm, v(171.06, 169.57) * mm]});
            skFitSpline(sketch, "E391", {"points": [v(171.06, 169.57) * mm, v(171.6, 172.33) * mm, v(171.86, 174.76) * mm, v(171.66, 174.96) * mm]});
            skFitSpline(sketch, "E392", {"points": [v(171.66, 174.96) * mm, v(171.45, 175.17) * mm, v(170.12, 175.34) * mm, v(168.72, 175.34) * mm]});
            skFitSpline(sketch, "E393", {"points": [v(168.72, 175.34) * mm, v(166.17, 175.34) * mm, v(166.16, 175.36) * mm, v(166.66, 178.04) * mm]});
            skFitSpline(sketch, "E394", {"points": [v(166.66, 178.04) * mm, v(167.46, 182.3) * mm, v(168.56, 183.52) * mm, v(171.6, 183.52) * mm]});
            skFitSpline(sketch, "E395", {"points": [v(171.6, 183.52) * mm, v(174.2, 183.52) * mm, v(174.36, 183.67) * mm, v(175.88, 187.8) * mm]});
            skFitSpline(sketch, "E396", {"points": [v(175.88, 187.8) * mm, v(180.22, 199.6) * mm, v(185.9, 202.36) * mm, v(189.42, 194.38) * mm]});
            skLineSegment(sketch, "E397", {"start": v(189.42, 194.38) * mm, "end": v(190.87, 191.12) * mm});
            skLineSegment(sketch, "E398", {"start": v(190.87, 191.12) * mm, "end": v(189.02, 187.88) * mm});
            skFitSpline(sketch, "E399", {"points": [v(189.02, 187.88) * mm, v(188, 186.1) * mm, v(187.16, 184.39) * mm, v(187.15, 184.08) * mm]});
            skFitSpline(sketch, "E400", {"points": [v(187.15, 184.08) * mm, v(187.15, 183.77) * mm, v(189.49, 183.52) * mm, v(192.35, 183.52) * mm]});
            skFitSpline(sketch, "E401", {"points": [v(192.35, 183.52) * mm, v(197.32, 183.52) * mm, v(197.56, 183.44) * mm, v(197.56, 181.77) * mm]});
            skFitSpline(sketch, "E402", {"points": [v(197.56, 181.77) * mm, v(197.56, 180.81) * mm, v(197.2, 178.97) * mm, v(196.74, 177.68) * mm]});
            skFitSpline(sketch, "E403", {"points": [v(196.74, 177.68) * mm, v(195.93, 175.35) * mm, v(195.92, 175.34) * mm, v(190.5, 175.34) * mm]});
            skFitSpline(sketch, "E404", {"points": [v(190.5, 175.34) * mm, v(186.52, 175.34) * mm, v(184.97, 175.06) * mm, v(184.67, 174.3) * mm]});
            skFitSpline(sketch, "E405", {"points": [v(184.67, 174.3) * mm, v(184.45, 173.72) * mm, v(183.86, 169.28) * mm, v(183.36, 164.44) * mm]});
            skFitSpline(sketch, "E406", {"points": [v(183.36, 164.44) * mm, v(182.36, 154.73) * mm, v(182.85, 148.74) * mm, v(184.7, 148.02) * mm]});
            skFitSpline(sketch, "E407", {"points": [v(184.7, 148.02) * mm, v(186.5, 147.34) * mm, v(192.17, 150.68) * mm, v(197.26, 155.44) * mm]});
            skFitSpline(sketch, "E408", {"points": [v(197.26, 155.44) * mm, v(199.78, 157.8) * mm, v(202.18, 159.72) * mm, v(202.6, 159.72) * mm]});
            skFitSpline(sketch, "E409", {"points": [v(202.6, 159.72) * mm, v(203.93, 159.72) * mm, v(204.3, 156.15) * mm, v(203.27, 153.17) * mm]});
            skFitSpline(sketch, "E410", {"points": [v(203.27, 153.17) * mm, v(200, 143.67) * mm, v(185.58, 134.51) * mm, v(177.34, 136.7) * mm]});
            skFitSpline(sketch, "E411", {"points": [v(177.34, 136.7) * mm, v(174.42, 137.49) * mm, v(172.08, 140.4) * mm, v(171.1, 144.47) * mm]});
            skFitSpline(sketch, "E412", {"points": [v(171.1, 144.47) * mm, v(170.29, 147.9) * mm, v(170.1, 147.99) * mm, v(167.19, 146.17) * mm]});
            skFitSpline(sketch, "E413", {"points": [v(167.19, 146.17) * mm, v(164.96, 144.78) * mm, v(163.48, 144.49) * mm, v(159.04, 144.55) * mm]});
            skFitSpline(sketch, "E414", {"points": [v(159.04, 144.55) * mm, v(153.88, 144.62) * mm, v(153.5, 144.5) * mm, v(150.9, 142.12) * mm]});
            skFitSpline(sketch, "E415", {"points": [v(150.9, 142.12) * mm, v(146.2, 137.83) * mm, v(142.2, 136.32) * mm, v(135.08, 136.14) * mm]});
            skFitSpline(sketch, "E416", {"points": [v(135.08, 136.14) * mm, v(131.6, 136.05) * mm, v(127.92, 136.25) * mm, v(126.9, 136.58) * mm]});
            skFitSpline(sketch, "E417", {"points": [v(154.17, 161.8) * mm, v(154.55, 165) * mm, v(154.4, 165.72) * mm, v(153.35, 166.13) * mm]});
            skFitSpline(sketch, "E418", {"points": [v(153.35, 166.13) * mm, v(151.52, 166.83) * mm, v(150.44, 165.37) * mm, v(150.55, 162.34) * mm]});
            skFitSpline(sketch, "E419", {"points": [v(150.55, 162.34) * mm, v(150.68, 159.12) * mm, v(152.04, 156.3) * mm, v(153.02, 157.28) * mm]});
            skFitSpline(sketch, "E420", {"points": [v(153.02, 157.28) * mm, v(153.4, 157.66) * mm, v(153.92, 159.7) * mm, v(154.17, 161.8) * mm]});
            skFitSpline(sketch, "E421", {"points": [v(-216, 222.42) * mm, v(-220.54, 224.72) * mm, v(-220.51, 230.49) * mm, v(-215.96, 232.8) * mm]});
            skFitSpline(sketch, "E422", {"points": [v(-215.96, 232.8) * mm, v(-213.66, 233.97) * mm, v(-210.56, 234.1) * mm, v(-184.95, 234.1) * mm]});
            skLineSegment(sketch, "E423", {"start": v(-184.95, 234.1) * mm, "end": v(-156.5, 234.1) * mm});
            skLineSegment(sketch, "E424", {"start": v(-156.5, 234.1) * mm, "end": v(-156.5, 236.32) * mm});
            skFitSpline(sketch, "E425", {"points": [v(-156.5, 236.32) * mm, v(-156.5, 240) * mm, v(-154.3, 244.46) * mm, v(-151.87, 245.72) * mm]});
            skFitSpline(sketch, "E426", {"points": [v(-151.87, 245.72) * mm, v(-149.38, 247) * mm, v(-4.22, 272.04) * mm, v(0.76, 272.04) * mm]});
            skFitSpline(sketch, "E427", {"points": [v(0.76, 272.04) * mm, v(4.02, 272.04) * mm, v(145.06, 248.14) * mm, v(150.09, 246.74) * mm]});
            skFitSpline(sketch, "E428", {"points": [v(150.09, 246.74) * mm, v(153.86, 245.69) * mm, v(156.5, 242.32) * mm, v(157.1, 237.8) * mm]});
            skLineSegment(sketch, "E429", {"start": v(157.1, 237.8) * mm, "end": v(157.58, 234.1) * mm});
            skLineSegment(sketch, "E430", {"start": v(157.58, 234.1) * mm, "end": v(185.64, 234.1) * mm});
            skFitSpline(sketch, "E431", {"points": [v(185.64, 234.1) * mm, v(214.56, 234.1) * mm, v(217.69, 233.82) * mm, v(219.15, 231.1) * mm]});
            skFitSpline(sketch, "E432", {"points": [v(219.15, 231.1) * mm, v(220.3, 228.93) * mm, v(220, 225.49) * mm, v(218.45, 223.59) * mm]});
            skLineSegment(sketch, "E433", {"start": v(218.45, 223.59) * mm, "end": v(217.03, 221.83) * mm});
            skLineSegment(sketch, "E434", {"start": v(217.03, 221.83) * mm, "end": v(1.44, 221.65) * mm});
            skFitSpline(sketch, "E435", {"points": [v(1.44, 221.65) * mm, v(-171.4, 221.51) * mm, v(-214.51, 221.66) * mm, v(-216, 222.42) * mm]});
            skLineSegment(sketch, "E436", {"start": v(-216, -140.24) * mm, "end": v(-216, -140.24) * mm});
            skSolve(sketch);
        }
        {
            var Q0;
            Q0=qSketchRegion(id+"F7",true);
            extrude(context, id + "F8", {"entities" : qUnion([Q0]), "operationType" : NewBodyOperationType.REMOVE, "oppositeDirection" : true, "depth" : 2 * mm});
        }
    });
